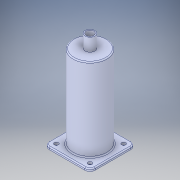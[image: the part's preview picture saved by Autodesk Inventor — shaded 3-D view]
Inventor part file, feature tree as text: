
AUTODESK INVENTOR PART (.ipt)
format: ipt  version: 2018 (Build 220112000, 112)  size: 194,048 bytes
history: native  units: in
note: dims shown in document units (in); Inventor stores cm internally (conversion verified against a paired STEP export)
features: extrude x5, sketch x3, projected_geometry x3, fillet x1, other x1
ambient origin geometry x8: Origin, YZ Plane, XZ Plane, XY Plane, X Axis, Y Axis, Z Axis, Center Point
bodies: Solid1 (feature_tree)
feature tree (13):
  extrude  "Extrusion1"  TaperAngle=0.0deg  [1 undecoded]
  sketch  "Sketch2"  dims[d4=0.3937in d5=0.0in d6=1.0in d7=0.0in]
  extrude  "Extrusion2"  Depth=1.0in TaperAngle=0.0deg
  extrude  "Extrusion3"  Depth=0.9252in
  sketch  "Sketch3"  dims[d8=2.0in d9=0.0in d10=0.9252in]
  extrude  "Extrusion4"  [1 undecoded]
  extrude  "Extrusion5"  [1 undecoded]
  fillet  "Fillet1"  [1 undecoded]
  sketch  "Sketch1"  dims[d0=0.0in d1=0.0in d2=0.0in d3=0.0in]
  projected_geometry  "Projected Loop1"
  projected_geometry  "Projected Loop2"
  projected_geometry  "Projected Loop3"
  other  "Ø8.0mm Dowel Hole1"
note: 4 required parameter values undecoded (feature->parameter linkage not recoverable at this tier; creation-order binding heuristic only, values carry confidence <= 0.55)
